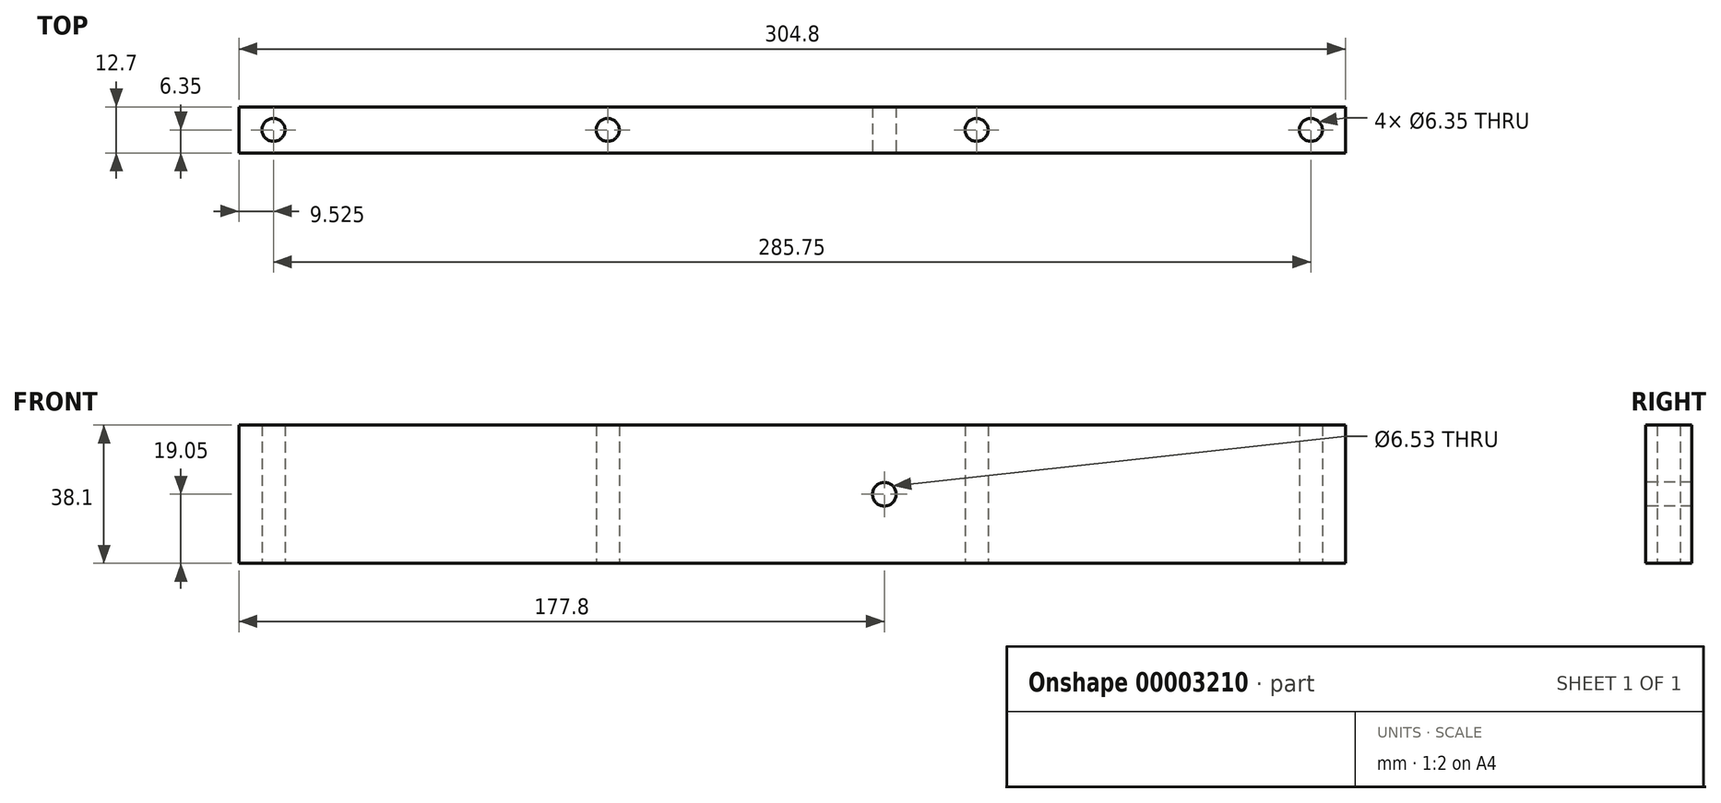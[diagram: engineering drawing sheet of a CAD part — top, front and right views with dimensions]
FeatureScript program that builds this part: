
annotation { "Feature Type Name" : "Feature", "Feature Type Description" : "" }
export const myFeature = defineFeature(function(context is Context, id is Id, definition is map)
    precondition{}
    {
        {
            var Q0;
            Q0=qCreatedBy(makeId("Front.planeOp"),FACE);
            var sketch = newSketch(context, id + "F0", { "sketchPlane" : qUnion([Q0])});
            skLineSegment(sketch, "E0", {"start": v(0, 0) * mm, "end": v(0, -38.1) * mm});
            skLineSegment(sketch, "E1", {"start": v(0, -38.1) * mm, "end": v(304.8, -38.1) * mm});
            skLineSegment(sketch, "E2", {"start": v(304.8, -38.1) * mm, "end": v(304.8, 0) * mm});
            skLineSegment(sketch, "E3", {"start": v(304.8, 0) * mm, "end": v(0, 0) * mm});
            skSolve(sketch);
        }
        {
            var Q0;
            Q0=qSketchRegion(id+"F0",true);
            extrude(context, id + "F1", {"entities" : qUnion([Q0]), "endBound" : BoundingType.SYMMETRIC, "depth" : 12.7 * mm});
        }
        {
            var Q0;
            Q0=makeQuery(id+"F1.opExtrude","SWEPT_FACE",FACE,{"disambiguationData":[OSD([sQuery(id+"F0.wireOp",EDGE,"E1")])]});
            var sketch = newSketch(context, id + "F2", { "sketchPlane" : qUnion([Q0])});
            skLineSegment(sketch, "E4", {"start": v(0, 0) * mm, "end": v(304.8, 0) * mm, "construction": true});
            skLineSegment(sketch, "E5", {"start": v(9.53, 6.35) * mm, "end": v(9.53, -6.35) * mm, "construction": true});
            skLineSegment(sketch, "E6", {"start": v(101.6, 6.35) * mm, "end": v(101.6, -6.35) * mm, "construction": true});
            skLineSegment(sketch, "E7", {"start": v(203.2, 6.35) * mm, "end": v(203.2, -6.35) * mm, "construction": true});
            skLineSegment(sketch, "E8", {"start": v(295.28, 6.35) * mm, "end": v(295.28, -6.35) * mm, "construction": true});
            skCircle(sketch, "E9", {"center": v(9.53, 0) * mm, "radius": 3.18 * mm});
            skCircle(sketch, "E10", {"center": v(101.6, 0) * mm, "radius": 3.18 * mm});
            skCircle(sketch, "E11", {"center": v(203.2, 0) * mm, "radius": 3.18 * mm});
            skCircle(sketch, "E12", {"center": v(295.28, 0) * mm, "radius": 3.18 * mm});
            skSolve(sketch);
        }
        {
            var Q0;
            Q0=qSketchRegion(id+"F2",true);
            extrude(context, id + "F3", {"entities" : qUnion([Q0]), "operationType" : NewBodyOperationType.REMOVE, "endBound" : BoundingType.THROUGH_ALL, "oppositeDirection" : true, "depth" : 25.4 * mm});
        }
        {
            var Q0;
            Q0=makeQuery(id+"F1.opExtrude","CAP_FACE",FACE,{"disambiguationData":[OSD([sQuery(id+"F0.wireOp",EDGE,"E0"),sQuery(id+"F0.wireOp",EDGE,"E1"),sQuery(id+"F0.wireOp",EDGE,"E2"),sQuery(id+"F0.wireOp",EDGE,"E3")])],"isStart":false});
            var sketch = newSketch(context, id + "F4", { "sketchPlane" : qUnion([Q0])});
            skLineSegment(sketch, "E13", {"start": v(0, -19.05) * mm, "end": v(304.8, -19.05) * mm, "construction": true});
            skLineSegment(sketch, "E14", {"start": v(177.8, 0) * mm, "end": v(177.8, -38.1) * mm, "construction": true});
            skCircle(sketch, "E15", {"center": v(177.8, -19.05) * mm, "radius": 3.26 * mm});
            skSolve(sketch);
        }
        {
            var Q0;
            Q0 = qSketchRegion(id + "F4", true);
            extrude(context, id + "F5", {"entities" : qUnion([Q0]), "operationType" : NewBodyOperationType.REMOVE, "endBound" : BoundingType.THROUGH_ALL, "oppositeDirection" : true, "depth" : 25.4 * mm});
        }
    });
